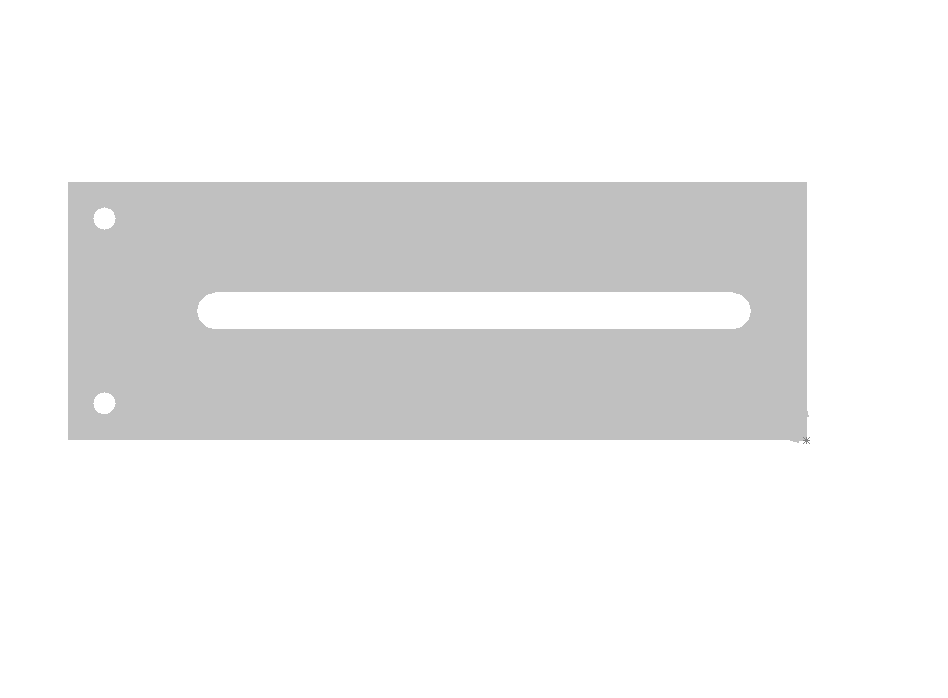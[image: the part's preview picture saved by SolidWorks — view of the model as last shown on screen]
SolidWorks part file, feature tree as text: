
SOLIDWORKS PART (.sldprt)
format: sldprt  version: not decoded by parser v0  size: 131,072 bytes
history: native  units: mm
features: plane x3, sketch x3, cut_extrude x2, extrude x1 (+5 scaffold rows collapsed)
feature tree (14):
  scaffold x5  (default folders/planes/origin — collapsed)
  plane  "Plane1"
  plane  "Plane2"
  plane  "Plane3"
  sketch  "Sketch1"  dims[c1.D6=5.0mm c1.D7=5.0mm c1.D3=2.5mm c1.D1=35.0mm c1.D2=100.0mm c2.D3=40.0mm c3.D3=90.0deg c4.D3=50.0mm c4.D4=18.75mm c5.D4=90.0deg c6.D4=18.75mm c7.D4=90.0deg c8.D4=5.0mm c8.D5=15.0mm c8.D8=2.5mm c8.D9=2.5mm c8.D3=10.0mm c9.D4=70.0mm]
  extrude  "Base-Extrude"  Depth=11mm
  sketch  "Sketch2"  dims[D1=3.0mm D2=12.5mm D3=5.0mm]
  cut_extrude  "Cut-Extrude1"  [1 undecoded]
  sketch  "Sketch3"  dims[D1=100.0mm D2=90.0mm D3=20.0mm]
  cut_extrude  "Cut-Extrude2"  Depth=5mm
decode coverage: 5 of 6 modeling features carry decoded parameters
note: 1 parameter value undecoded
note: suppression state not decoded; provenance and decode notes live in map.json
